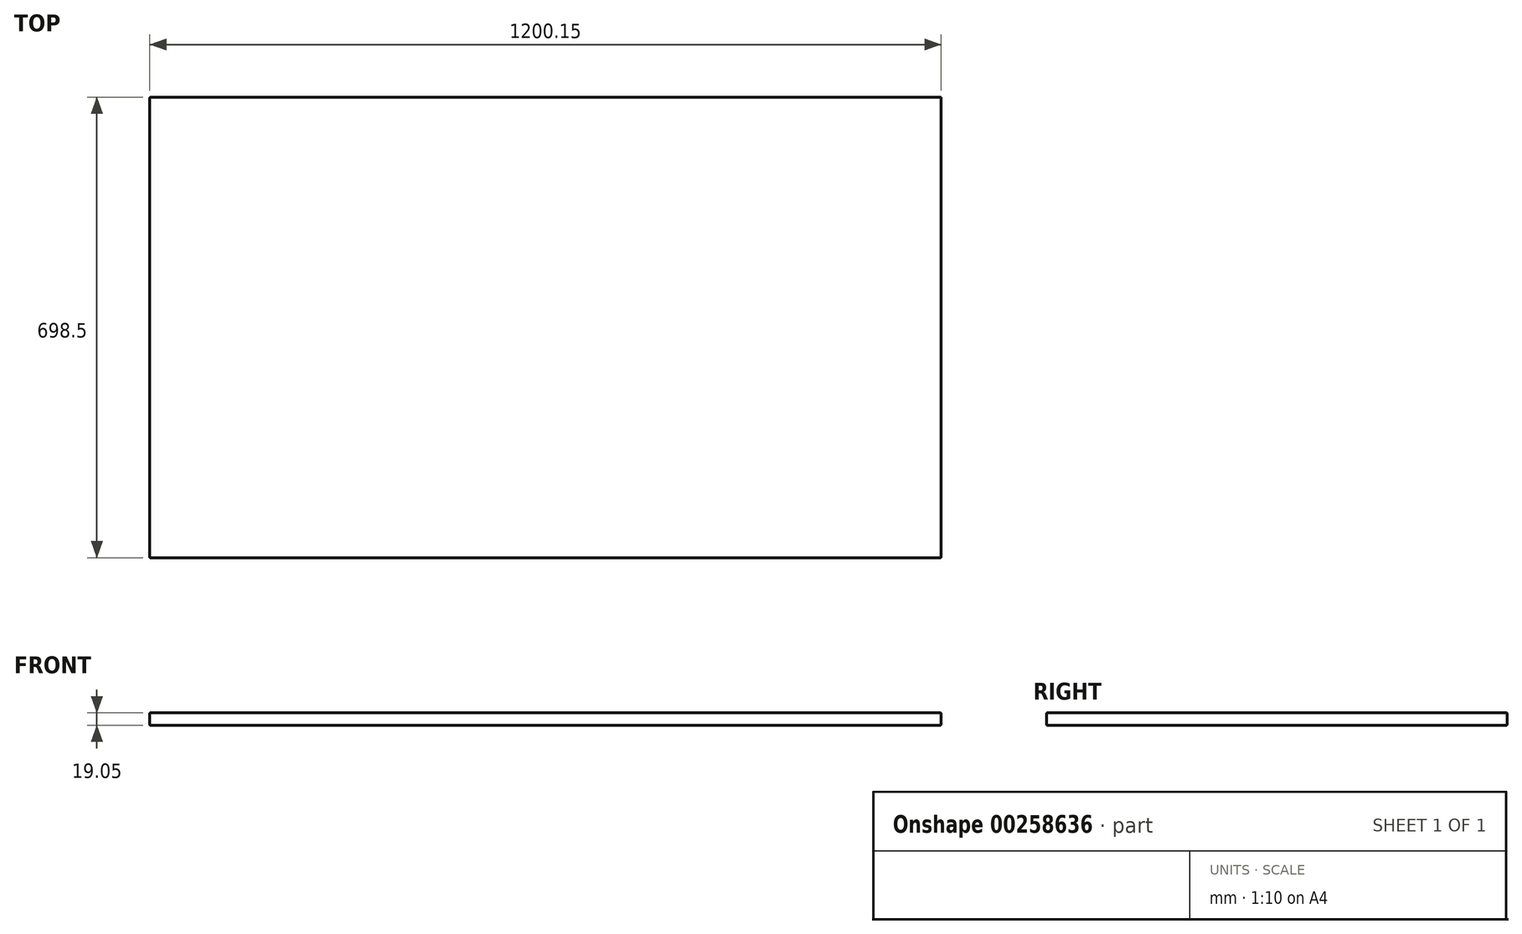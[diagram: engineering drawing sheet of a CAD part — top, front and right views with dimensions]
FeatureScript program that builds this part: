
annotation { "Feature Type Name" : "Feature", "Feature Type Description" : "" }
export const myFeature = defineFeature(function(context is Context, id is Id, definition is map)
    precondition{}
    {
        {
            var Q0;
            Q0=qCreatedBy(makeId("Top.planeOp"),FACE);
            var sketch = newSketch(context, id + "F0", { "sketchPlane" : qUnion([Q0])});
            skLineSegment(sketch, "E0.bottom", {"start": v(0, 0) * mm, "end": v(1200.15, 0) * mm});
            skLineSegment(sketch, "E0.top", {"start": v(0, 698.5) * mm, "end": v(1200.15, 698.5) * mm});
            skLineSegment(sketch, "E0.left", {"start": v(0, 0) * mm, "end": v(0, 698.5) * mm});
            skLineSegment(sketch, "E0.right", {"start": v(1200.15, 0) * mm, "end": v(1200.15, 698.5) * mm});
            skSolve(sketch);
        }
        {
            var Q0;
            Q0 = qSketchRegion(id + "F0", true);
            extrude(context, id + "F1", {"entities" : qUnion([Q0]), "depth" : 19.05 * mm});
        }
        {
            var Q0;
            Q0=makeQuery(id+"F1.opExtrude","SWEPT_FACE",FACE,{"disambiguationData":[OSD([sQuery(id+"F0.wireOp",EDGE,"E0.bottom")])]});
            var Q1;
            Q1=makeQuery(id+"F1.opExtrude","CAP_EDGE",EDGE,{"disambiguationData":[OSD([sQuery(id+"F0.wireOp",EDGE,"E0.right")])],"isStart":true});
            var Q2;
            Q2=makeQuery(id+"F1.opExtrude","SWEPT_FACE",FACE,{"disambiguationData":[OSD([sQuery(id+"F0.wireOp",EDGE,"E0.top")])]});
            var Q3;
            Q3=makeQuery(id+"F1.opExtrude","SWEPT_FACE",FACE,{"disambiguationData":[OSD([sQuery(id+"F0.wireOp",EDGE,"E0.right")])]});
            var Q4;
            Q4=makeQuery(id+"F1.opExtrude","SWEPT_FACE",FACE,{"disambiguationData":[OSD([sQuery(id+"F0.wireOp",EDGE,"E0.left")])]});
            fillet(context, id + "F2", {"entities" : qUnion([Q0, Q1, Q2, Q3, Q4]), "radius" : 1.27 * mm, "tangentPropagation" : true, "allowEdgeOverflow" : false});
        }
    });
